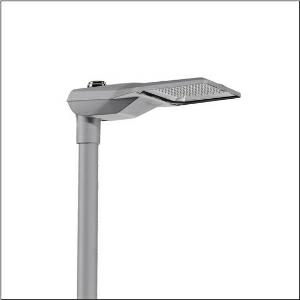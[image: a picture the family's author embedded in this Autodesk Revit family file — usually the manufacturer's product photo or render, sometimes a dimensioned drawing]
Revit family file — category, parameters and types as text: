
# Revit family: streetlight_sl_21_midi___p1_0a_5xe7a37n08mb_bed1
name_source: partatom
category: Lighting Fixtures
units: mm (PartAtom-declared; Revit-internal decimal feet)

## family parameters
Cut with Voids When Loaded = No
Host = Face
Light Source = No
Part Type = Normal
Room Calculation Point = No
Round Connector Dimension = Use Diameter
Shared = No

## types (1)
- --- (1 x LED, 18270 lm, 136 W, 3000K)
    Apparent Load = 136 VA
    CIE Flux Codes = 21 50 90 100 100
    Color Rendering = 70
    Color Temperature = 3000K
    Default Elevation = 1800 mm
    Description = Streetlight SL 21 midi, mast luminaire, primary light control with lens, of PMMA, primary optical cover: cover, of toughened safety glass, transparent, light distribution: P1.0a, light emission: direct distribution, primary light characteristic: asymmetric, installation type: side-entry, LED, 3G 2.5mm², High Power LED, rated luminous flux: 18.270lm, luminous efficacy: 134lm/W, light colour: 730, colour temperature: 3000K, control gear: NEMA (7pin), control: overheat protection, pre-setting: linear dimming characteristic, constant luminous flux control, time-dependent luminous flux control, flexible luminous flux parameterisation, mains connection: 220..240V, AC, 50/60Hz, connection cable pre-assembled, cable length: 12,5m, wiring characteristics: H05VV-F, start of lifetime: 136W, end of service life: 142W, reduction: 61W, luminaire housing, of diecast aluminium (EN AC-44300), powder-coated, Siteco® metallic grey (DB 702S), corrosivity category C5 mid according to DIN EN ISO 12944, multi-level sealing system, sealing non-destructively replaceable, inclination adjustable: 0°, 5°, 10°, 15°, length: 644mm, width: 335mm, height: 110mm, spigot size: 42mm (side-entry), mounting height: 4..8m, protection rating (complete): IP66, insulation class (complete): insulation class I (protective earthing), certification: CE, ENEC, ENEC+, VDE, impact resistance: IK09, permissible operating ambient temperature for outdoor applications: -40..+50°C, standard-compliant lighting for roads and squares, packaging unit: 1 piece

Light Distribution: P1.0a
    Height = 111 mm
    Lamp = 1 x LED
    Lamp Light Flux = 18270 lm
    Lamp Power = 136 W
    Lamp count = 1
    Length = 644 mm
    Luminous efficacy = 134 lm/W
    Manufacturer = Siteco
    ModVariant = No
    Model = 5XE7A37N08MB
    Number of Poles = 1
    OnlyDefault = Yes
    Power Factor = 1
    Product Name = Streetlight SL 21 midi | P1.0a
    Product group = mast luminaire | pylon top
    ProductGroupID = 6100
    Protection Class = Protection class I
    Protection Degree = IP 66
    RLX_Detail_Level = 1
    RLX_Emergency_Light_Flux = 0 lm
    RLX_Emergency_Type = 0
    RLX_Emergency_Type_DB = No
    RlxData = <blob elided: 101761 chars, md5=66af8e07>
    Socket = socket
    Standby Power = 0 W
    System Light Flux = 18270 lm
    System Power = 136 W
    Type Comments = factory setting: luminous flux: 100 % | dim-lin: 254 | 695 mA
    Type Image = l_1294377.jpg
    URL = http://relux.com
    VarID = @adj_131952
    Voltage = 0 V
    Weight = 0.00 kg
    Width = 336 mm

## geometry (parser evidence)
native form markers: Blend x4, Sweep x10
no freeform markers — native parametric forms only
